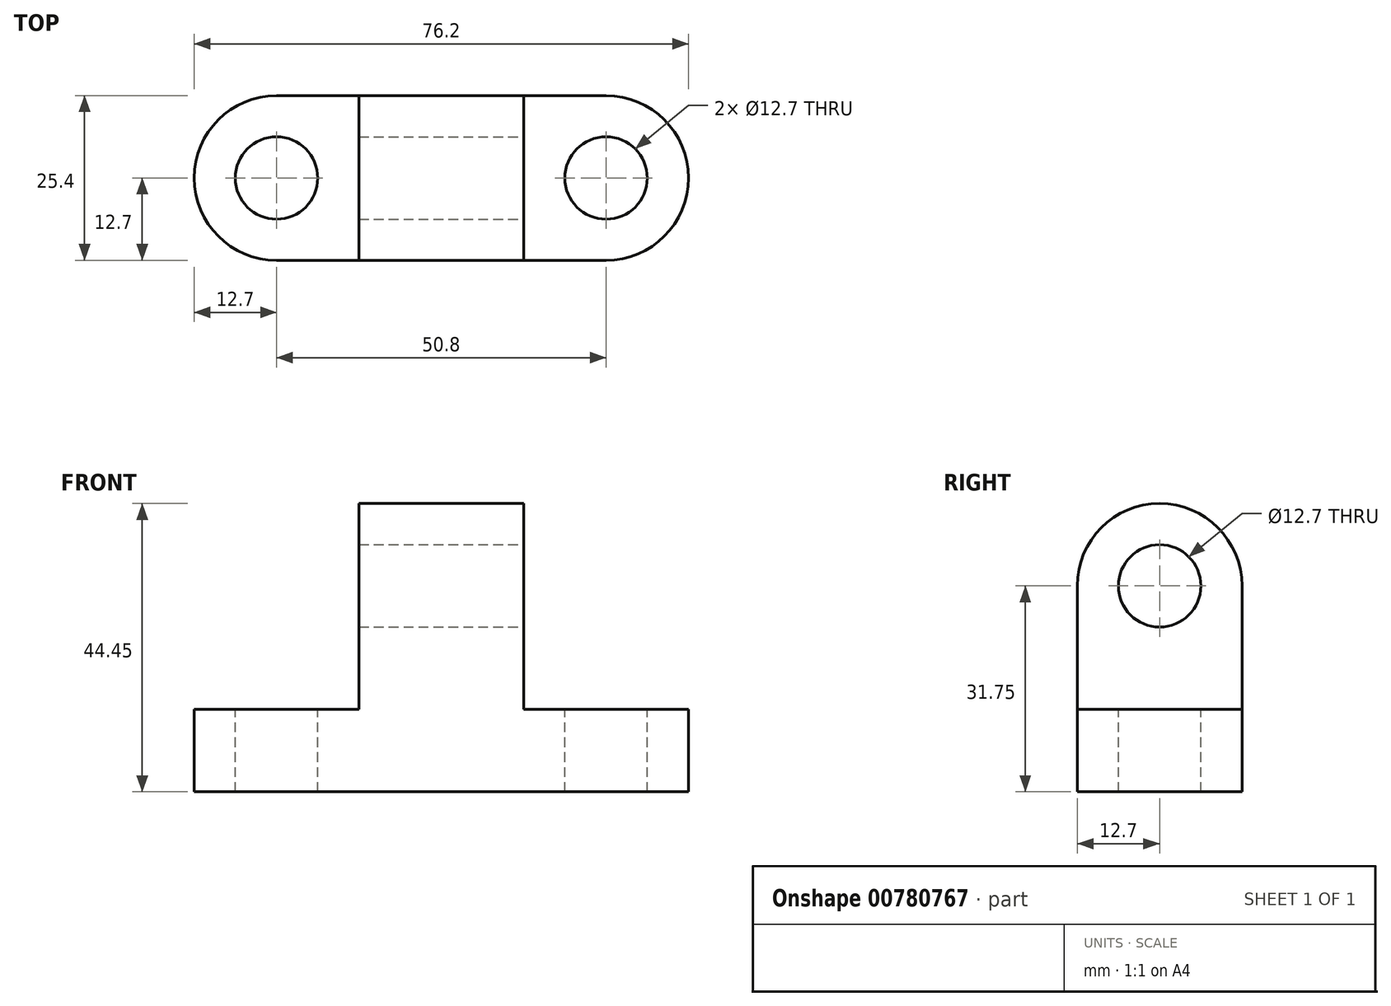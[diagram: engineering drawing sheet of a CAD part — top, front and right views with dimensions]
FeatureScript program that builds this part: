
annotation { "Feature Type Name" : "Feature", "Feature Type Description" : "" }
export const myFeature = defineFeature(function(context is Context, id is Id, definition is map)
    precondition{}
    {
        {
            var Q0;
            Q0=qCreatedBy(makeId("Front.planeOp"),FACE);
            var sketch = newSketch(context, id + "F0", { "sketchPlane" : qUnion([Q0])});
            skLineSegment(sketch, "E0", {"start": v(0, 0) * mm, "end": v(76.2, 0) * mm});
            skLineSegment(sketch, "E1", {"start": v(76.2, 0) * mm, "end": v(76.2, 12.7) * mm});
            skLineSegment(sketch, "E2", {"start": v(76.2, 12.7) * mm, "end": v(50.8, 12.7) * mm});
            skLineSegment(sketch, "E3", {"start": v(50.8, 12.7) * mm, "end": v(50.8, 44.45) * mm});
            skLineSegment(sketch, "E4", {"start": v(50.8, 44.45) * mm, "end": v(25.4, 44.45) * mm});
            skLineSegment(sketch, "E5", {"start": v(25.4, 44.45) * mm, "end": v(25.4, 12.7) * mm});
            skLineSegment(sketch, "E6", {"start": v(25.4, 12.7) * mm, "end": v(0, 12.7) * mm});
            skLineSegment(sketch, "E7", {"start": v(0, 12.7) * mm, "end": v(0, 0) * mm});
            skSolve(sketch);
        }
        {
            var Q0;
            Q0 = qSketchRegion(id + "F0", true);
            extrude(context, id + "F1", {"entities" : qUnion([Q0]), "depth" : 25.4 * mm, "offsetDistance" : 25.4 * mm});
        }
        {
            var Q0;
            Q0=makeQuery(id+"F1.opExtrude","CAP_EDGE",EDGE,{"disambiguationData":[OSD([sQuery(id+"F0.wireOp",EDGE,"E4")])],"isStart":false});
            var Q1;
            Q1=makeQuery(id+"F1.opExtrude","CAP_EDGE",EDGE,{"disambiguationData":[OSD([sQuery(id+"F0.wireOp",EDGE,"E4")])],"isStart":true});
            var Q2;
            Q2=makeQuery(id+"F1.opExtrude","CAP_EDGE",EDGE,{"disambiguationData":[OSD([sQuery(id+"F0.wireOp",EDGE,"E7")])],"isStart":false});
            var Q3;
            Q3=makeQuery(id+"F1.opExtrude","CAP_EDGE",EDGE,{"disambiguationData":[OSD([sQuery(id+"F0.wireOp",EDGE,"E1")])],"isStart":false});
            var Q4;
            Q4=makeQuery(id+"F1.opExtrude","CAP_EDGE",EDGE,{"disambiguationData":[OSD([sQuery(id+"F0.wireOp",EDGE,"E1")])],"isStart":true});
            var Q5;
            Q5=makeQuery(id+"F1.opExtrude","CAP_EDGE",EDGE,{"disambiguationData":[OSD([sQuery(id+"F0.wireOp",EDGE,"E7")])],"isStart":true});
            fillet(context, id + "F2", {"entities" : qUnion([Q0, Q1, Q2, Q3, Q4, Q5]), "radius" : 12.7 * mm, "tangentPropagation" : true, "allowEdgeOverflow" : false});
        }
        {
            var Q0;
            Q0=makeQuery(id+"F1.opExtrude","SWEPT_FACE",FACE,{"disambiguationData":[OSD([sQuery(id+"F0.wireOp",EDGE,"E3")])]});
            var sketch = newSketch(context, id + "F3", { "sketchPlane" : qUnion([Q0])});
            skCircle(sketch, "E8", {"center": v(-12.7, 31.75) * mm, "radius": 6.35 * mm});
            skSolve(sketch);
        }
        {
            var Q0;
            Q0 = qSketchRegion(id + "F3", true);
            extrude(context, id + "F4", {"entities" : qUnion([Q0]), "operationType" : NewBodyOperationType.REMOVE, "oppositeDirection" : true, "depth" : 25.4 * mm, "offsetDistance" : 25.4 * mm});
        }
        {
            var Q0;
            Q0=makeQuery(id+"F1.opExtrude","SWEPT_FACE",FACE,{"disambiguationData":[OSD([sQuery(id+"F0.wireOp",EDGE,"E6")])]});
            var sketch = newSketch(context, id + "F5", { "sketchPlane" : qUnion([Q0])});
            skCircle(sketch, "E9", {"center": v(12.7, -12.7) * mm, "radius": 6.35 * mm});
            skSolve(sketch);
        }
        {
            var Q0;
            Q0 = qSketchRegion(id + "F5", true);
            extrude(context, id + "F6", {"entities" : qUnion([Q0]), "operationType" : NewBodyOperationType.REMOVE, "oppositeDirection" : true, "depth" : 25.4 * mm, "offsetDistance" : 25.4 * mm});
        }
        {
            var Q0;
            Q0=makeQuery(id+"F1.opExtrude","SWEPT_FACE",FACE,{"disambiguationData":[OSD([sQuery(id+"F0.wireOp",EDGE,"E2")])]});
            var sketch = newSketch(context, id + "F7", { "sketchPlane" : qUnion([Q0])});
            skCircle(sketch, "E10", {"center": v(63.5, -12.7) * mm, "radius": 6.35 * mm});
            skSolve(sketch);
        }
        {
            var Q0;
            Q0 = qSketchRegion(id + "F7", true);
            extrude(context, id + "F8", {"entities" : qUnion([Q0]), "operationType" : NewBodyOperationType.REMOVE, "oppositeDirection" : true, "depth" : 25.4 * mm, "offsetDistance" : 25.4 * mm});
        }
    });
